# Revit family: IS_Connect_E8234_BIM_DE
name_source: partatom
category: Plumbing Fixtures
revit_build: Autodesk Revit MEP 2014 (Build: 20130308_1515(x64)
units: mm (PartAtom-declared; Revit-internal decimal feet)

## types (4) — shared parameters
Accessories = www.idealstandard.de\ersatzteile
AreaUnits = millimeters
Assembly Code = C1030200
AssetType = Fixed
Brand = Ideal Standard
CodePerformance = DIN EN 997, CL1-6-VRII, DIN EN 33
ConnectionType = Plumbing
DurationUnit = year
ExpectedLife = 25
Features = Connect compact close coupled back-to-wall bowl, wash-down
GrossWeight = 0
IfcExportAs = IfcSanitaryTerminalType
IfcExportType = TOILETPAN
InstallationInstructions = www.idealstandard.de\produkte
LinearUnits = millimeters
ManufacturerURL = www.idealstandard.com
ModelReference = Connect compact close coupled back-to-wall bowl, wash-down
NBSDescription = WC pans
NBSReference = 45-30-70/384
NominalHeight = 775 mm  [stored 2.54265 ft]
NominalLength = 660 mm
NominalWidth = 360 mm  [stored 1.1811 ft]
PanColor = White
PanMaterial = Vitreous china
PanMounting = BackToWall
ProductInformation = www.idealstandard.de/produkte
Shape = Sculptured
Size = 360x660x775mm
Space = Internal
ToiletPanType = WashDown
ToiletType = Other
URL = www.idealstandard.com
Uniclass2015Code = Pr_40_20_93_94
Uniclass2015Title = WC pans
Uniclass2015Version = Products v1.1
Version = 1
VolumeUnits = Litres
WarrantyDescription = Manufacturers Warranty
WarrantyDurationUnit = year
zero-valued in all types: CWFU, Cost, Default Elevation, HWFU, SpilloverLevel, WFU

## per-type parameters (varying)
| type | (E7127-E7128)seat | (E7723-E7724)seat | BIMObjectName | BarCode | Description | Finish | Model | ModelNumber | Name | NettWeight |
| E823401 - Connect compact close coupled back-to-wall bowl, wash-down (E7723-E7724)Seat | No | Yes | ISI_IdealStandard_WcPans_Connect_E823401 | 5017830448716 | E823401 Connect compact close coupled back-to-wall bowl, wash-down | white | E823401 | E823401 | WcPans_Connect_E823401_IdealStandard | 29,957 kg |
| E823401 - Connect compact close coupled back-to-wall bowl, wash-down (E7127-E7128)Seat | Yes | No | ISI_IdealStandard_WcPans_Connect_E823401 | 5017830448716 | E823401 Connect compact close coupled back-to-wall bowl, wash-down | white | E823401 | E823401 | WcPans_Connect_E823401_IdealStandard | 29,957 kg |
| E8234MA - Connect compact close coupled back-to-wall bowl, wash-down(E7127-E7128)Seat | Yes | No | ISI_IdealStandard_WcPans_Connect_E8234MA | 5017830448983 | E8234MA Connect compact close coupled back-to-wall bowl, wash-down | white with ideal plus | E8234MA | E8234MA | WcPans_Connect_E8234MA_IdealStandard | 26 kg |
| E8234MA - Connect compact close coupled back-to-wall bowl, wash-down(E7723-E7724)Seat | No | Yes | ISI_IdealStandard_WcPans_Connect_E8234MA | 5017830448983 | E8234MA Connect compact close coupled back-to-wall bowl, wash-down | white with ideal plus | E8234MA | E8234MA | WcPans_Connect_E8234MA_IdealStandard | 26 kg |

note: [stored X ft] marks values corroborated as IEEE doubles in the binary element streams (Revit-internal decimal feet)

## geometry (parser evidence)
native form markers: Blend x2, Sweep x9
no freeform markers — native parametric forms only
